# Revit family: Pipefitting_IBP_Conex_MaxiPro_45°Bend_MP5041
name_source: partatom
category: Pipe Fittings
units: mm (PartAtom-declared; Revit-internal decimal feet)

## family parameters
Always vertical = No
Cut with Voids When Loaded = No
OmniClass Number = 23.65.00.00
OmniClass Title = Supply and Distribution of Liquids and Gases
Part Type = Elbow
Round Connector Dimension = Use Diameter
Shared = No
Work Plane-Based = No

## types (8) — shared parameters
Angle = 45.00°
Application = Air conditioning & refrigeration
Assembly Code = D20
AssetType = Fixed
BIMObjectName = PipeFitting_IBP_Conex_MaxiPro_45°Bend_MP5041
ClassificationName = Uniclass2015
ClassificationValue = Pr_65_52_63_18
Description = 45° Bend
ExpectedServiceLifeYears = 25
FittingType = 45° Bend
FluidTemperatureMax = 121 °C
FluidTemperatureMin = -40 °C
IfcExportAs = IfcPipeFitting
IfcExportType = IfcPipeFittingType
Keynote = S
Manufacturer = Conex Banninger
ManufacturerName = IBP
Material = Copper, C12200
MaterialType = Refrigerant Grade Copper, C12200
MaxHydrostaticPressure = 48 bar
NBSDescription = Copper pipeline fittings
NBSObjectName = IBP - Copper pipeline fittings
NBSReference = 90-10-65/315
ORingTemperatureRange = -40°C to 140°C
PipeConnectorType = Press x Press
PressJawCompatability = MaxiPro Jaws supplied by Rothenberger
SealType = HNBR
Shape = Cylindrical
SurfaceFinish = Natural
URL = http://www.conexbanninger.com
WarrantyDescription = Product Guarantee
WarrantyDurationMonths = 60
Weight = 0.00 kg
_BimstoreBibleVersion = 14
_CurrentRevision = 1
_DistributedBy = www.bimmepaus.com.au/
zero-valued in all types: NominalDepth, NominalHeight, NominalLength, _BimSpecGuid

## per-type parameters (varying)
| type | A_Length | B_TubeStopLocation | Bead_OD | C_Bend_Radius | D1_OD | DN | L2_TubeStop | L2_TubeStop_Formula | MainBody_Dia | Model | ModelNumber | ModelReference | ProductCode | Size | Type Comments |
| MP5041 0020000 1/4" | 24 mm | 6 mm  [stored 0.019685 ft] | 2 mm  [stored 0.00656168 ft] | 13 mm | 8 mm  [stored 0.0262467 ft] | 6 mm  [stored 0.019685 ft] | 8 mm  [stored 0.0262467 ft] | 16 mm  [stored 0.0524934 ft] | 6 mm  [stored 0.019685 ft] | MP5041 0020000 | MP5041 0020000 | 1/4" Connection | MP5041 0020000 | 1/4" Connection | 1/4" Connection |
| MP5041 0030000 3/8" | 26 mm | 8 mm  [stored 0.0262467 ft] | 2 mm  [stored 0.00656168 ft] | 18 mm  [stored 0.0590551 ft] | 12 mm  [stored 0.0393701 ft] | 10 mm  [stored 0.0328084 ft] | 7 mm  [stored 0.0229659 ft] | 19 mm | 10 mm  [stored 0.0328084 ft] | MP5041 0030000 | MP5041 0030000 | 3/8" Connection | MP5041 0030000 | 3/8" Connection | 3/8" Connection |
| MP5041 0040000 1/2" | 24 mm | 7 mm  [stored 0.0229659 ft] | 3 mm  [stored 0.00984252 ft] | 15 mm  [stored 0.0492126 ft] | 15 mm  [stored 0.0492126 ft] | 13 mm | 7 mm  [stored 0.0229659 ft] | 17 mm | 13 mm | MP5041 0040000 | MP5041 0040000 | 1/2" Connection | MP5041 0040000 | 1/2" Connection | 1/2" Connection |
| MP5041 0050000 5/8" | 28 mm | 7 mm  [stored 0.0229659 ft] | 3 mm  [stored 0.00984252 ft] | 20 mm | 19 mm | 16 mm  [stored 0.0524934 ft] | 8 mm  [stored 0.0262467 ft] | 20 mm | 16 mm  [stored 0.0524934 ft] | MP5041 0050000 | MP5041 0050000 | 5/8" Connection | MP5041 0050000 | 5/8" Connection | 5/8" Connection |
| MP5041 0060000 3/4" | 32 mm | 10 mm  [stored 0.0328084 ft] | 3 mm  [stored 0.00984252 ft] | 23 mm | 22 mm | 19 mm | 10 mm  [stored 0.0328084 ft] | 22 mm | 19 mm | MP5041 0060000 | MP5041 0060000 | 3/4" Connection | MP5041 0060000 | 3/4" Connection | 3/4" Connection |
| MP5041 0070000 7/8" | 34 mm | 10 mm  [stored 0.0328084 ft] | 3 mm  [stored 0.00984252 ft] | 28 mm | 25 mm  [stored 0.082021 ft] | 22 mm | 10 mm  [stored 0.0328084 ft] | 24 mm | 22 mm | MP5041 0070000 | MP5041 0070000 | 7/8" Connection | MP5041 0070000 | 7/8" Connection | 7/8" Connection |
| MP5041 0080000 1" | 36 mm | 12 mm  [stored 0.0393701 ft] | 3 mm  [stored 0.00984252 ft] | 31 mm | 29 mm | 26 mm | 10 mm  [stored 0.0328084 ft] | 26 mm | 26 mm | MP5041 0080000 | MP5041 0080000 | 1" Connection | MP5041 0080000 | 1" Connection | 1" Connection |
| MP5041 0090000 1 1/8" | 40 mm | 14 mm  [stored 0.0459318 ft] | 3 mm  [stored 0.00984252 ft] | 35 mm  [stored 0.114829 ft] | 32 mm | 29 mm | 10 mm  [stored 0.0328084 ft] | 29 mm | 29 mm | MP5041 0090000 | MP5041 0090000 | 1 1/8" Connection | MP5041 0090000 | 1 1/8" Connection | 1 1/8" Connection |

note: [stored X ft] marks values corroborated as IEEE doubles in the binary element streams (Revit-internal decimal feet)

## geometry (parser evidence)
native form markers: Blend x2, Sweep x7
no freeform markers — native parametric forms only
